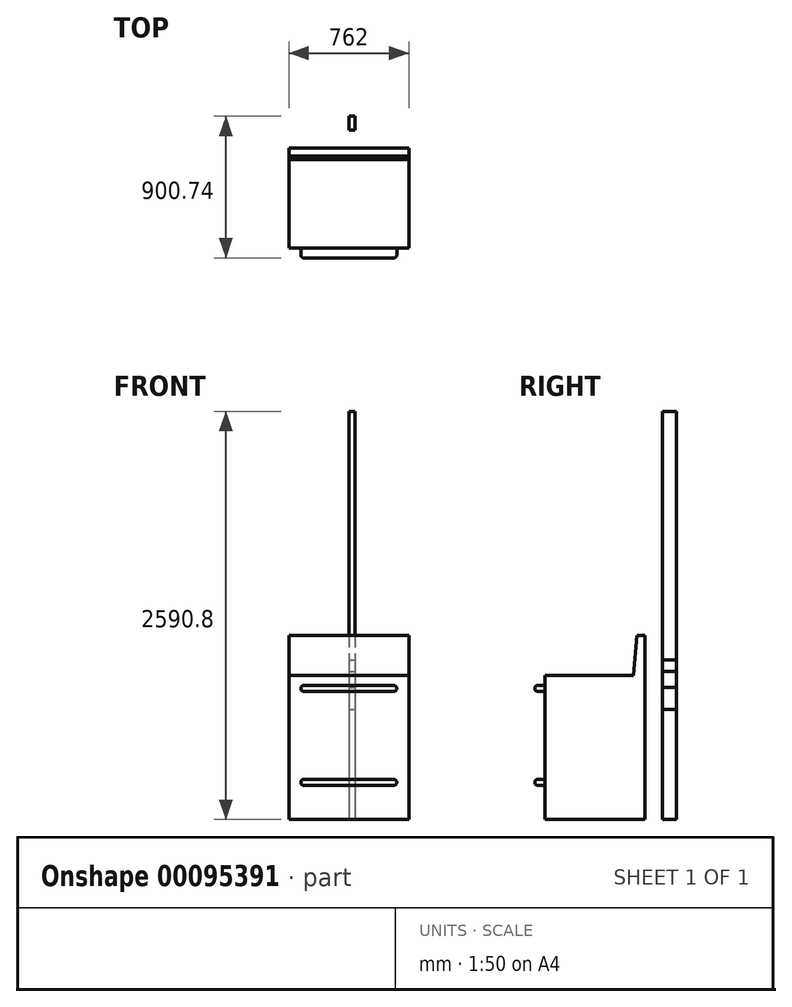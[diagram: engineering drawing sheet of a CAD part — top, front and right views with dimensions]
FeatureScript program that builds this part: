
annotation { "Feature Type Name" : "Feature", "Feature Type Description" : "" }
export const myFeature = defineFeature(function(context is Context, id is Id, definition is map)
    precondition{}
    {
        {
            var Q0;
            Q0=qCreatedBy(makeId("Right.planeOp"),FACE);
            var sketch = newSketch(context, id + "F0", { "sketchPlane" : qUnion([Q0])});
            skLineSegment(sketch, "E0", {"start": v(0, 0) * mm, "end": v(0, 1168.4) * mm});
            skLineSegment(sketch, "E1", {"start": v(0, 1168.4) * mm, "end": v(-50.8, 1168.4) * mm});
            skLineSegment(sketch, "E2", {"start": v(-50.8, 1168.4) * mm, "end": v(-73.02, 914.4) * mm});
            skLineSegment(sketch, "E3", {"start": v(-73.02, 914.4) * mm, "end": v(-635, 914.4) * mm});
            skLineSegment(sketch, "E4", {"start": v(-635, 914.4) * mm, "end": v(-635, 0) * mm});
            skLineSegment(sketch, "E5", {"start": v(-635, 0) * mm, "end": v(0, 0) * mm});
            skSolve(sketch);
        }
        {
            var Q0;
            Q0=makeQuery(id+"F0.imprint","IMPRINT",FACE,{"disambiguationData":[TD([[makeQuery(id+"F0.imprint","IMPRINT",EDGE,{"derivedFrom":sQuery(id+"F0.wireOp",EDGE,"E0")}),1.0]])]});
            extrude(context, id + "F1", {"entities" : qUnion([Q0]), "depth" : 762 * mm, "symmetric" : true});
        }
        {
            var Q0;
            Q0=qCreatedBy(makeId("Right.planeOp"),FACE);
            var sketch = newSketch(context, id + "F2", { "sketchPlane" : qUnion([Q0])});
            skLineSegment(sketch, "E6.bottom", {"start": v(-635, 850.9) * mm, "end": v(-698.5, 850.9) * mm});
            skLineSegment(sketch, "E6.top", {"start": v(-635, 812.8) * mm, "end": v(-698.5, 812.8) * mm});
            skLineSegment(sketch, "E6.left", {"start": v(-635, 850.9) * mm, "end": v(-635, 812.8) * mm});
            skLineSegment(sketch, "E6.right", {"start": v(-698.5, 850.9) * mm, "end": v(-698.5, 812.8) * mm});
            skLineSegment(sketch, "E7.bottom", {"start": v(-635, 254) * mm, "end": v(-698.5, 254) * mm});
            skLineSegment(sketch, "E7.top", {"start": v(-635, 215.9) * mm, "end": v(-698.5, 215.9) * mm});
            skLineSegment(sketch, "E7.left", {"start": v(-635, 254) * mm, "end": v(-635, 215.9) * mm});
            skLineSegment(sketch, "E7.right", {"start": v(-698.5, 254) * mm, "end": v(-698.5, 215.9) * mm});
            skSolve(sketch);
        }
        {
            var Q0;
            Q0=makeQuery(id+"F2.imprint","IMPRINT",FACE,{"disambiguationData":[TD([[makeQuery(id+"F2.imprint","IMPRINT",EDGE,{"derivedFrom":sQuery(id+"F2.wireOp",EDGE,"E6.bottom")}),1.0]])]});
            var Q1;
            Q1=makeQuery(id+"F2.imprint","IMPRINT",FACE,{"disambiguationData":[TD([[makeQuery(id+"F2.imprint","IMPRINT",EDGE,{"derivedFrom":sQuery(id+"F2.wireOp",EDGE,"E7.bottom")}),1.0]])]});
            extrude(context, id + "F3", {"entities" : qUnion([Q0, Q1]), "operationType" : NewBodyOperationType.ADD, "depth" : 609.6 * mm, "symmetric" : true});
        }
        {
            var Q0;
            Q0=makeQuery(id+"F3.opExtrude","SWEPT_EDGE",EDGE,{"disambiguationData":[OSD([sQuery(id+"F2.wireOp",EDGE,"E6.bottom"),sQuery(id+"F2.wireOp",EDGE,"E6.right")])]});
            var Q1;
            Q1=makeQuery(id+"F3.opExtrude","SWEPT_EDGE",EDGE,{"disambiguationData":[OSD([sQuery(id+"F2.wireOp",EDGE,"E6.top"),sQuery(id+"F2.wireOp",EDGE,"E6.right")])]});
            var Q2;
            Q2=makeQuery(id+"F3.opExtrude","CAP_EDGE",EDGE,{"disambiguationData":[OSD([sQuery(id+"F2.wireOp",EDGE,"E6.right")])],"isStart":true});
            var Q3;
            Q3=makeQuery(id+"F3.opExtrude","CAP_EDGE",EDGE,{"disambiguationData":[OSD([sQuery(id+"F2.wireOp",EDGE,"E6.right")])],"isStart":false});
            var Q4;
            Q4=makeQuery(id+"F3.opExtrude","CAP_EDGE",EDGE,{"disambiguationData":[OSD([sQuery(id+"F2.wireOp",EDGE,"E6.bottom")])],"isStart":false});
            var Q5;
            Q5=makeQuery(id+"F3.opExtrude","CAP_EDGE",EDGE,{"disambiguationData":[OSD([sQuery(id+"F2.wireOp",EDGE,"E6.top")])],"isStart":false});
            var Q6;
            Q6=makeQuery(id+"F3.opExtrude","CAP_EDGE",EDGE,{"disambiguationData":[OSD([sQuery(id+"F2.wireOp",EDGE,"E6.bottom")])],"isStart":true});
            var Q7;
            Q7=makeQuery(id+"F3.opExtrude","CAP_EDGE",EDGE,{"disambiguationData":[OSD([sQuery(id+"F2.wireOp",EDGE,"E6.top")])],"isStart":true});
            var Q8;
            Q8=makeQuery(id+"F3.opExtrude","CAP_EDGE",EDGE,{"disambiguationData":[OSD([sQuery(id+"F2.wireOp",EDGE,"E7.bottom")])],"isStart":true});
            var Q9;
            Q9=makeQuery(id+"F3.opExtrude","CAP_EDGE",EDGE,{"disambiguationData":[OSD([sQuery(id+"F2.wireOp",EDGE,"E7.top")])],"isStart":true});
            var Q10;
            Q10=makeQuery(id+"F3.opExtrude","SWEPT_EDGE",EDGE,{"disambiguationData":[OSD([sQuery(id+"F2.wireOp",EDGE,"E7.top"),sQuery(id+"F2.wireOp",EDGE,"E7.right")])]});
            var Q11;
            Q11=makeQuery(id+"F3.opExtrude","CAP_EDGE",EDGE,{"disambiguationData":[OSD([sQuery(id+"F2.wireOp",EDGE,"E7.right")])],"isStart":true});
            var Q12;
            Q12=makeQuery(id+"F3.opExtrude","CAP_EDGE",EDGE,{"disambiguationData":[OSD([sQuery(id+"F2.wireOp",EDGE,"E7.right")])],"isStart":false});
            var Q13;
            Q13=makeQuery(id+"F3.opExtrude","SWEPT_EDGE",EDGE,{"disambiguationData":[OSD([sQuery(id+"F2.wireOp",EDGE,"E7.bottom"),sQuery(id+"F2.wireOp",EDGE,"E7.right")])]});
            var Q14;
            Q14=makeQuery(id+"F3.opExtrude","CAP_EDGE",EDGE,{"disambiguationData":[OSD([sQuery(id+"F2.wireOp",EDGE,"E7.bottom")])],"isStart":false});
            var Q15;
            Q15=makeQuery(id+"F3.opExtrude","CAP_EDGE",EDGE,{"disambiguationData":[OSD([sQuery(id+"F2.wireOp",EDGE,"E7.top")])],"isStart":false});
            fillet(context, id + "F4", {"entities" : qUnion([Q0, Q1, Q2, Q3, Q4, Q5, Q6, Q7, Q8, Q9, Q10, Q11, Q12, Q13, Q14, Q15]), "radius" : 19.05 * mm, "tangentPropagation" : true, "allowEdgeOverflow" : false});
        }
        {
            var Q0;
            Q0=qCreatedBy(makeId("Top.planeOp"),FACE);
            var sketch = newSketch(context, id + "F5", { "sketchPlane" : qUnion([Q0])});
            skLineSegment(sketch, "E8.bottom", {"start": v(0, 202.24) * mm, "end": v(38.1, 202.24) * mm});
            skLineSegment(sketch, "E8.top", {"start": v(0, 113.34) * mm, "end": v(38.1, 113.34) * mm});
            skLineSegment(sketch, "E8.left", {"start": v(0, 202.24) * mm, "end": v(0, 113.34) * mm});
            skLineSegment(sketch, "E8.right", {"start": v(38.1, 202.24) * mm, "end": v(38.1, 113.34) * mm});
            skSolve(sketch);
        }
        {
            var Q0;
            Q0=makeQuery(id+"F5.imprint","IMPRINT",FACE,{"disambiguationData":[TD([[makeQuery(id+"F5.imprint","IMPRINT",EDGE,{"derivedFrom":sQuery(id+"F5.wireOp",EDGE,"E8.bottom")}),-1.0]])]});
            extrude(context, id + "F6", {"entities" : qUnion([Q0]), "depth" : 838.2 * mm});
        }
        {
            var Q0;
            Q0=makeQuery(id+"F5.imprint","IMPRINT",FACE,{"disambiguationData":[TD([[makeQuery(id+"F5.imprint","IMPRINT",EDGE,{"derivedFrom":sQuery(id+"F5.wireOp",EDGE,"E8.bottom")}),-1.0]])]});
            extrude(context, id + "F7", {"entities" : qUnion([Q0]), "depth" : 2590.8 * mm});
        }
        {
            var Q0;
            Q0=makeQuery(id+"F5.imprint","IMPRINT",FACE,{"disambiguationData":[TD([[makeQuery(id+"F5.imprint","IMPRINT",EDGE,{"derivedFrom":sQuery(id+"F5.wireOp",EDGE,"E8.bottom")}),-1.0]])]});
            extrude(context, id + "F8", {"entities" : qUnion([Q0]), "depth" : 939.8 * mm});
        }
        {
            var Q0;
            Q0=makeQuery(id+"F5.imprint","IMPRINT",FACE,{"disambiguationData":[TD([[makeQuery(id+"F5.imprint","IMPRINT",EDGE,{"derivedFrom":sQuery(id+"F5.wireOp",EDGE,"E8.bottom")}),-1.0]])]});
            extrude(context, id + "F9", {"entities" : qUnion([Q0]), "depth" : 1011.3 * mm});
        }
        {
            var Q0;
            Q0=makeQuery(id+"F5.imprint","IMPRINT",FACE,{"disambiguationData":[TD([[makeQuery(id+"F5.imprint","IMPRINT",EDGE,{"derivedFrom":sQuery(id+"F5.wireOp",EDGE,"E8.bottom")}),-1.0]])]});
            extrude(context, id + "F10", {"entities" : qUnion([Q0]), "depth" : 698.5 * mm});
        }
    });
